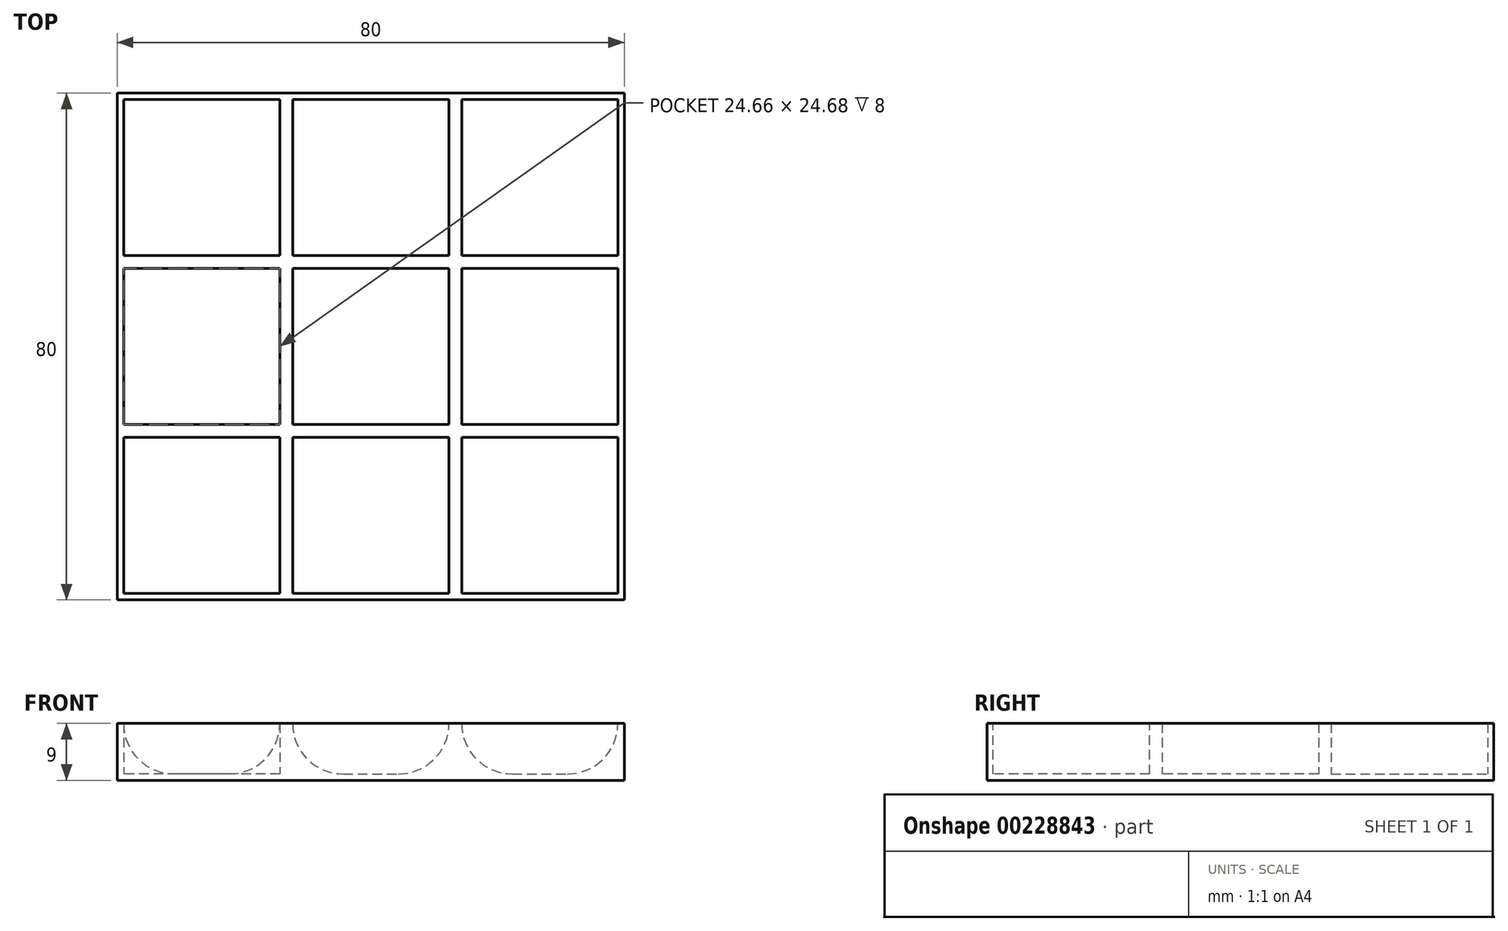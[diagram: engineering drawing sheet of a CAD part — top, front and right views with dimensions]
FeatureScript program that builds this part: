
annotation { "Feature Type Name" : "Feature", "Feature Type Description" : "" }
export const myFeature = defineFeature(function(context is Context, id is Id, definition is map)
    precondition{}
    {
        {
            var Q0;
            Q0=qCreatedBy(makeId("Top.planeOp"),FACE);
            var sketch = newSketch(context, id + "F0", { "sketchPlane" : qUnion([Q0])});
            skLineSegment(sketch, "E0.bottom", {"start": v(40, -40) * mm, "end": v(-40, -40) * mm});
            skLineSegment(sketch, "E0.top", {"start": v(40, 40) * mm, "end": v(-40, 40) * mm});
            skLineSegment(sketch, "E0.left", {"start": v(40, -40) * mm, "end": v(40, 40) * mm});
            skLineSegment(sketch, "E0.right", {"start": v(-40, -40) * mm, "end": v(-40, 40) * mm});
            skPoint(sketch, "E0.middle", {"position": v(0, 0) * mm});
            skPoint(sketch, "E1", {"position": v(-13.34, 13.34) * mm});
            skPoint(sketch, "E2", {"position": v(13.34, 13.34) * mm});
            skPoint(sketch, "E3", {"position": v(13.34, -13.34) * mm});
            skPoint(sketch, "E4", {"position": v(-13.34, -13.34) * mm});
            skLineSegment(sketch, "E5", {"start": v(-13.34, 13.34) * mm, "end": v(-13.34, 40) * mm, "construction": true});
            skLineSegment(sketch, "E6", {"start": v(-13.34, 13.34) * mm, "end": v(-40, 13.34) * mm, "construction": true});
            skLineSegment(sketch, "E7", {"start": v(-40, -13.34) * mm, "end": v(-13.34, -13.34) * mm});
            skLineSegment(sketch, "E8", {"start": v(-13.34, 13.34) * mm, "end": v(-13.34, -13.34) * mm, "construction": true});
            skLineSegment(sketch, "E9", {"start": v(-13.34, -13.34) * mm, "end": v(-13.34, -40) * mm, "construction": true});
            skLineSegment(sketch, "E10", {"start": v(13.34, -40) * mm, "end": v(13.34, -13.34) * mm, "construction": true});
            skLineSegment(sketch, "E11", {"start": v(13.34, -13.34) * mm, "end": v(-13.34, -13.34) * mm, "construction": true});
            skLineSegment(sketch, "E12", {"start": v(13.34, -13.34) * mm, "end": v(40, -13.34) * mm, "construction": true});
            skLineSegment(sketch, "E13", {"start": v(13.34, -13.34) * mm, "end": v(13.34, 13.34) * mm, "construction": true});
            skLineSegment(sketch, "E14", {"start": v(40, 13.34) * mm, "end": v(13.34, 13.34) * mm, "construction": true});
            skLineSegment(sketch, "E15", {"start": v(13.34, 13.34) * mm, "end": v(13.34, 40) * mm, "construction": true});
            skLineSegment(sketch, "E16", {"start": v(-13.34, 13.34) * mm, "end": v(13.34, 13.34) * mm, "construction": true});
            skLineSegment(sketch, "E17", {"start": v(40, 40) * mm, "end": v(13.34, 13.34) * mm, "construction": true});
            skLineSegment(sketch, "E18", {"start": v(-40, 40) * mm, "end": v(-13.34, 13.34) * mm, "construction": true});
            skLineSegment(sketch, "E19", {"start": v(-13.34, -13.34) * mm, "end": v(-40, -40) * mm, "construction": true});
            skLineSegment(sketch, "E20", {"start": v(13.34, -13.34) * mm, "end": v(40, -40) * mm, "construction": true});
            skLineSegment(sketch, "E21", {"start": v(-40, 0) * mm, "end": v(-13.34, 0) * mm, "construction": true});
            skLineSegment(sketch, "E22", {"start": v(0, 40) * mm, "end": v(0, 13.34) * mm, "construction": true});
            skLineSegment(sketch, "E23", {"start": v(0, -13.34) * mm, "end": v(0, -40) * mm, "construction": true});
            skLineSegment(sketch, "E24", {"start": v(40, 0) * mm, "end": v(13.34, 0) * mm, "construction": true});
            skPoint(sketch, "E25", {"position": v(0, 26.67) * mm});
            skPoint(sketch, "E26", {"position": v(26.67, 0) * mm});
            skPoint(sketch, "E27", {"position": v(26.67, -26.67) * mm});
            skPoint(sketch, "E28", {"position": v(0, -26.67) * mm});
            skPoint(sketch, "E29", {"position": v(-26.67, -26.67) * mm});
            skPoint(sketch, "E30", {"position": v(-26.67, 0) * mm});
            skPoint(sketch, "E31", {"position": v(-26.67, 26.67) * mm});
            skLineSegment(sketch, "E32.bottom", {"start": v(-14.34, 14.34) * mm, "end": v(-39, 14.34) * mm});
            skLineSegment(sketch, "E32.top", {"start": v(-14.34, 39) * mm, "end": v(-39, 39) * mm});
            skLineSegment(sketch, "E32.left", {"start": v(-14.34, 14.34) * mm, "end": v(-14.34, 39) * mm});
            skLineSegment(sketch, "E32.right", {"start": v(-39, 14.34) * mm, "end": v(-39, 39) * mm});
            skLineSegment(sketch, "E33.bottom", {"start": v(-14.34, 12.34) * mm, "end": v(-39, 12.34) * mm});
            skLineSegment(sketch, "E33.top", {"start": v(-14.34, -12.34) * mm, "end": v(-39, -12.34) * mm});
            skLineSegment(sketch, "E33.left", {"start": v(-14.34, 12.34) * mm, "end": v(-14.34, -12.34) * mm});
            skLineSegment(sketch, "E33.right", {"start": v(-39, 12.34) * mm, "end": v(-39, -12.34) * mm});
            skLineSegment(sketch, "E34.bottom", {"start": v(-14.34, -14.34) * mm, "end": v(-39, -14.34) * mm});
            skLineSegment(sketch, "E34.top", {"start": v(-14.34, -39) * mm, "end": v(-39, -39) * mm});
            skLineSegment(sketch, "E34.left", {"start": v(-14.34, -14.34) * mm, "end": v(-14.34, -39) * mm});
            skLineSegment(sketch, "E34.right", {"start": v(-39, -14.34) * mm, "end": v(-39, -39) * mm});
            skLineSegment(sketch, "E35.bottom", {"start": v(-12.34, 39) * mm, "end": v(12.34, 39) * mm});
            skLineSegment(sketch, "E35.top", {"start": v(-12.34, 14.34) * mm, "end": v(12.34, 14.34) * mm});
            skLineSegment(sketch, "E35.left", {"start": v(-12.34, 39) * mm, "end": v(-12.34, 14.34) * mm});
            skLineSegment(sketch, "E35.right", {"start": v(12.34, 39) * mm, "end": v(12.34, 14.34) * mm});
            skLineSegment(sketch, "E36.bottom", {"start": v(-12.34, 12.34) * mm, "end": v(12.34, 12.34) * mm});
            skLineSegment(sketch, "E36.top", {"start": v(-12.34, -12.34) * mm, "end": v(12.34, -12.34) * mm});
            skLineSegment(sketch, "E36.left", {"start": v(-12.34, 12.34) * mm, "end": v(-12.34, -12.34) * mm});
            skLineSegment(sketch, "E36.right", {"start": v(12.34, 12.34) * mm, "end": v(12.34, -12.34) * mm});
            skLineSegment(sketch, "E37.bottom", {"start": v(-12.34, -14.34) * mm, "end": v(12.34, -14.34) * mm});
            skLineSegment(sketch, "E37.top", {"start": v(-12.34, -39) * mm, "end": v(12.34, -39) * mm});
            skLineSegment(sketch, "E37.left", {"start": v(-12.34, -14.34) * mm, "end": v(-12.34, -39) * mm});
            skLineSegment(sketch, "E37.right", {"start": v(12.34, -14.34) * mm, "end": v(12.34, -39) * mm});
            skLineSegment(sketch, "E38.bottom", {"start": v(14.34, -14.34) * mm, "end": v(39, -14.34) * mm});
            skLineSegment(sketch, "E38.top", {"start": v(14.34, -39) * mm, "end": v(39, -39) * mm});
            skLineSegment(sketch, "E38.left", {"start": v(14.34, -14.34) * mm, "end": v(14.34, -39) * mm});
            skLineSegment(sketch, "E38.right", {"start": v(39, -14.34) * mm, "end": v(39, -39) * mm});
            skLineSegment(sketch, "E39.bottom", {"start": v(14.34, -12.34) * mm, "end": v(39, -12.34) * mm});
            skLineSegment(sketch, "E39.top", {"start": v(14.34, 12.34) * mm, "end": v(39, 12.34) * mm});
            skLineSegment(sketch, "E39.left", {"start": v(14.34, -12.34) * mm, "end": v(14.34, 12.34) * mm});
            skLineSegment(sketch, "E39.right", {"start": v(39, -12.34) * mm, "end": v(39, 12.34) * mm});
            skPoint(sketch, "E40", {"position": v(26.67, 26.67) * mm});
            skLineSegment(sketch, "E41.bottom", {"start": v(14.34, 14.34) * mm, "end": v(39, 14.34) * mm});
            skLineSegment(sketch, "E41.top", {"start": v(14.34, 39) * mm, "end": v(39, 39) * mm});
            skLineSegment(sketch, "E41.left", {"start": v(14.34, 14.34) * mm, "end": v(14.34, 39) * mm});
            skLineSegment(sketch, "E41.right", {"start": v(39, 14.34) * mm, "end": v(39, 39) * mm});
            skSolve(sketch);
        }
        {
            var Q0;
            {var subQ1=sQuery(id+"F0.wireOp",EDGE,"E0.bottom");Q0=makeQuery(id+"F0.imprint","IMPRINT",FACE,{"disambiguationData":[TD([[makeQuery(id+"F0.imprint","IMPRINT",EDGE,{"derivedFrom":subQ1}),-1.0]])]});}
            extrude(context, id + "F1", {"entities" : qUnion([Q0]), "depth" : 8 * mm});
        }
        {
            var Q0;
            Q0=makeQuery(id+"F0.imprint","IMPRINT",FACE,{"disambiguationData":[TD([[makeQuery(id+"F0.imprint","IMPRINT",EDGE,{"derivedFrom":sQuery(id+"F0.wireOp",EDGE,"E34.bottom")}),1.0]])]});
            var Q1;
            Q1=makeQuery(id+"F0.imprint","IMPRINT",FACE,{"disambiguationData":[TD([[makeQuery(id+"F0.imprint","IMPRINT",EDGE,{"derivedFrom":sQuery(id+"F0.wireOp",EDGE,"E33.bottom")}),1.0]])]});
            var Q2;
            Q2=makeQuery(id+"F0.imprint","IMPRINT",FACE,{"disambiguationData":[TD([[makeQuery(id+"F0.imprint","IMPRINT",EDGE,{"derivedFrom":sQuery(id+"F0.wireOp",EDGE,"E32.bottom")}),-1.0]])]});
            var Q3;
            Q3=makeQuery(id+"F0.imprint","IMPRINT",FACE,{"disambiguationData":[TD([[makeQuery(id+"F0.imprint","IMPRINT",EDGE,{"derivedFrom":sQuery(id+"F0.wireOp",EDGE,"E36.bottom")}),-1.0]])]});
            var Q4;
            Q4=makeQuery(id+"F0.imprint","IMPRINT",FACE,{"disambiguationData":[TD([[makeQuery(id+"F0.imprint","IMPRINT",EDGE,{"derivedFrom":sQuery(id+"F0.wireOp",EDGE,"E37.bottom")}),-1.0]])]});
            var Q5;
            Q5=makeQuery(id+"F0.imprint","IMPRINT",FACE,{"disambiguationData":[TD([[makeQuery(id+"F0.imprint","IMPRINT",EDGE,{"derivedFrom":sQuery(id+"F0.wireOp",EDGE,"E38.bottom")}),-1.0]])]});
            var Q6;
            Q6=makeQuery(id+"F0.imprint","IMPRINT",FACE,{"disambiguationData":[TD([[makeQuery(id+"F0.imprint","IMPRINT",EDGE,{"derivedFrom":sQuery(id+"F0.wireOp",EDGE,"E39.bottom")}),1.0]])]});
            var Q7;
            Q7=makeQuery(id+"F0.imprint","IMPRINT",FACE,{"disambiguationData":[TD([[makeQuery(id+"F0.imprint","IMPRINT",EDGE,{"derivedFrom":sQuery(id+"F0.wireOp",EDGE,"E35.bottom")}),-1.0]])]});
            var Q8;
            Q8=makeQuery(id+"F0.imprint","IMPRINT",FACE,{"disambiguationData":[TD([[makeQuery(id+"F0.imprint","IMPRINT",EDGE,{"derivedFrom":sQuery(id+"F0.wireOp",EDGE,"E41.bottom")}),1.0]])]});
            var Q9;
            {var subQ1=sQuery(id+"F0.wireOp",EDGE,"E0.bottom");Q9=makeQuery(id+"F0.imprint","IMPRINT",FACE,{"disambiguationData":[TD([[makeQuery(id+"F0.imprint","IMPRINT",EDGE,{"derivedFrom":subQ1}),-1.0]])]});}
            extrude(context, id + "F2", {"entities" : qUnion([Q0, Q1, Q2, Q3, Q4, Q5, Q6, Q7, Q8, Q9]), "operationType" : NewBodyOperationType.ADD, "oppositeDirection" : true, "depth" : 1 * mm});
        }
        {
            var Q0;
            Q0=makeQuery(id+"F1.opExtrude","CAP_EDGE",EDGE,{"disambiguationData":[OSD([sQuery(id+"F0.wireOp",EDGE,"E38.left")])],"isStart":true});
            var Q1;
            Q1=makeQuery(id+"F1.opExtrude","CAP_EDGE",EDGE,{"disambiguationData":[OSD([sQuery(id+"F0.wireOp",EDGE,"E39.left")])],"isStart":true});
            var Q2;
            Q2=makeQuery(id+"F1.opExtrude","CAP_EDGE",EDGE,{"disambiguationData":[OSD([sQuery(id+"F0.wireOp",EDGE,"E41.left")])],"isStart":true});
            var Q3;
            Q3=makeQuery(id+"F1.opExtrude","CAP_EDGE",EDGE,{"disambiguationData":[OSD([sQuery(id+"F0.wireOp",EDGE,"E35.left")])],"isStart":true});
            var Q4;
            Q4=makeQuery(id+"F1.opExtrude","CAP_EDGE",EDGE,{"disambiguationData":[OSD([sQuery(id+"F0.wireOp",EDGE,"E36.left")])],"isStart":true});
            var Q5;
            Q5=makeQuery(id+"F1.opExtrude","CAP_EDGE",EDGE,{"disambiguationData":[OSD([sQuery(id+"F0.wireOp",EDGE,"E37.left")])],"isStart":true});
            var Q6;
            Q6=makeQuery(id+"F1.opExtrude","CAP_EDGE",EDGE,{"disambiguationData":[OSD([sQuery(id+"F0.wireOp",EDGE,"E34.right")])],"isStart":true});
            var Q7;
            Q7=makeQuery(id+"F1.opExtrude","CAP_EDGE",EDGE,{"disambiguationData":[OSD([sQuery(id+"F0.wireOp",EDGE,"E33.right")])],"isStart":true});
            var Q8;
            Q8=makeQuery(id+"F1.opExtrude","CAP_EDGE",EDGE,{"disambiguationData":[OSD([sQuery(id+"F0.wireOp",EDGE,"E32.right")])],"isStart":true});
            var Q9;
            Q9=makeQuery(id+"F1.opExtrude","CAP_EDGE",EDGE,{"disambiguationData":[OSD([sQuery(id+"F0.wireOp",EDGE,"E37.right")])],"isStart":true});
            var Q10;
            Q10=makeQuery(id+"F1.opExtrude","CAP_EDGE",EDGE,{"disambiguationData":[OSD([sQuery(id+"F0.wireOp",EDGE,"E36.right")])],"isStart":true});
            var Q11;
            Q11=makeQuery(id+"F1.opExtrude","CAP_EDGE",EDGE,{"disambiguationData":[OSD([sQuery(id+"F0.wireOp",EDGE,"E35.right")])],"isStart":true});
            var Q12;
            Q12=makeQuery(id+"F1.opExtrude","CAP_EDGE",EDGE,{"disambiguationData":[OSD([sQuery(id+"F0.wireOp",EDGE,"E32.left")])],"isStart":true});
            var Q13;
            Q13=makeQuery(id+"F1.opExtrude","CAP_EDGE",EDGE,{"disambiguationData":[OSD([sQuery(id+"F0.wireOp",EDGE,"E33.left")])],"isStart":true});
            var Q14;
            Q14=makeQuery(id+"F1.opExtrude","CAP_EDGE",EDGE,{"disambiguationData":[OSD([sQuery(id+"F0.wireOp",EDGE,"E34.left")])],"isStart":true});
            var Q15;
            Q15=makeQuery(id+"F1.opExtrude","CAP_EDGE",EDGE,{"disambiguationData":[OSD([sQuery(id+"F0.wireOp",EDGE,"E41.right")])],"isStart":true});
            var Q16;
            Q16=makeQuery(id+"F1.opExtrude","CAP_EDGE",EDGE,{"disambiguationData":[OSD([sQuery(id+"F0.wireOp",EDGE,"E39.right")])],"isStart":true});
            var Q17;
            Q17=makeQuery(id+"F1.opExtrude","CAP_EDGE",EDGE,{"disambiguationData":[OSD([sQuery(id+"F0.wireOp",EDGE,"E38.right")])],"isStart":true});
            fillet(context, id + "F3", {"entities" : qUnion([Q0, Q1, Q2, Q3, Q4, Q5, Q6, Q7, Q8, Q9, Q10, Q11, Q12, Q13, Q14, Q15, Q16, Q17]), "radius" : 8 * mm, "tangentPropagation" : true, "allowEdgeOverflow" : false});
        }
    });
